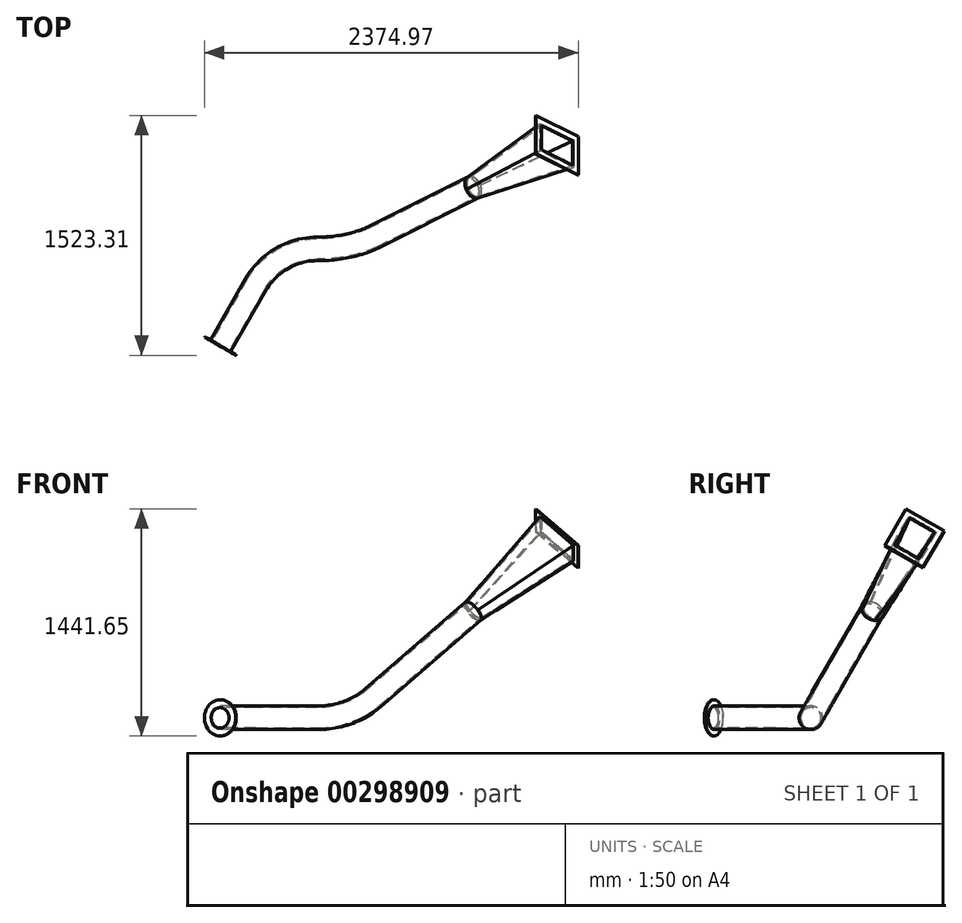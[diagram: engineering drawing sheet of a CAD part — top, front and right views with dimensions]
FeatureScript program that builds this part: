
annotation { "Feature Type Name" : "Feature", "Feature Type Description" : "" }
export const myFeature = defineFeature(function(context is Context, id is Id, definition is map)
    precondition{}
    {
        {
            var Q0;
            Q0=qCreatedBy(makeId("Right.planeOp"),FACE);
            var sketch = newSketch(context, id + "F0", { "sketchPlane" : qUnion([Q0])});
            skLineSegment(sketch, "E0", {"start": v(0, 0) * mm, "end": v(-42.12, 24.32) * mm});
            skSolve(sketch);
        }
        {
            var Q0;
            Q0=sQuery(id+"F0.wireOp",VERTEX,"E0.start");
            var Q1;
            Q1=sQuery(id+"F0.wireOp",EDGE,"E0");
            cPlane(context, id + "F1", {"entities" : qUnion([Q0, Q1]), "cplaneType" : CPlaneType.LINE_POINT, "offset" : 25 * mm, "width" : 150 * mm, "height" : 150 * mm});
        }
        {
            var Q0;
            Q0=qCreatedBy(makeId("Top.planeOp"),FACE);
            var sketch = newSketch(context, id + "F2", { "sketchPlane" : qUnion([Q0])});
            skArc(sketch, "E1", {"start": v(0, 0) * mm, "mid": v(-225, -60.29) * mm, "end": v(-389.71, -225) * mm});
            skLineSegment(sketch, "E2", {"start": v(0, 0) * mm, "end": v(0, -450) * mm, "construction": true});
            skLineSegment(sketch, "E3", {"start": v(-389.71, -225) * mm, "end": v(0, -450) * mm, "construction": true});
            skLineSegment(sketch, "E4", {"start": v(-389.71, -225) * mm, "end": v(-614.71, -614.71) * mm});
            skSolve(sketch);
        }
        {
            var Q0;
            Q0=qCreatedBy(id+"F1.planeOp",FACE);
            var sketch = newSketch(context, id + "F3", { "sketchPlane" : qUnion([Q0])});
            skArc(sketch, "E5", {"start": v(0, 0) * mm, "mid": v(191.34, 38.06) * mm, "end": v(353.55, 146.45) * mm});
            skLineSegment(sketch, "E6", {"start": v(0, 0) * mm, "end": v(0, 500) * mm, "construction": true});
            skLineSegment(sketch, "E7", {"start": v(0, 500) * mm, "end": v(353.55, 146.45) * mm, "construction": true});
            skLineSegment(sketch, "E8", {"start": v(353.55, 146.45) * mm, "end": v(989.95, 782.84) * mm});
            skSolve(sketch);
        }
        {
            var Q0;
            Q0=qCreatedBy(makeId("Right.planeOp"),FACE);
            var sketch = newSketch(context, id + "F4", { "sketchPlane" : qUnion([Q0])});
            skCircle(sketch, "E9", {"center": v(0, 0) * mm, "radius": 75 * mm});
            skSolve(sketch);
        }
        {
            var Q0;
            Q0=makeQuery(id+"F4.imprint","IMPRINT",FACE,{"disambiguationData":[TD([[makeQuery(id+"F4.imprint","IMPRINT",EDGE,{"derivedFrom":sQuery(id+"F4.wireOp",EDGE,"E9")}),1.0]])]});
            var Q1;
            Q1=sQuery(id+"F2.wireOp",EDGE,"E1");
            var Q2;
            Q2=sQuery(id+"F2.wireOp",EDGE,"E4");
            sweep(context, id + "F5", {"profiles" : qUnion([Q0]), "path" : qUnion([Q1, Q2])});
        }
        {
            var Q0;
            Q0=makeQuery(id+"F5.opSweep","CAP_FACE",FACE,{"disambiguationData":[OSD([sQuery(id+"F2.wireOp",VERTEX,"E1.start"),sQuery(id+"F4.wireOp",EDGE,"E9")])],"isStart":true});
            var Q1;
            Q1=sQuery(id+"F3.wireOp",EDGE,"E5");
            var Q2;
            Q2=sQuery(id+"F3.wireOp",EDGE,"E8");
            sweep(context, id + "F6", {"operationType" : NewBodyOperationType.ADD, "profiles" : qUnion([Q0]), "path" : qUnion([Q1, Q2])});
        }
        {
            var Q0;
            Q0=makeQuery(id+"F6.opSweep","CAP_FACE",FACE,{"disambiguationData":[OSD([sQuery(id+"F2.wireOp",VERTEX,"E1.start"),sQuery(id+"F3.wireOp",VERTEX,"E8.end"),sQuery(id+"F4.wireOp",EDGE,"E9")])],"isStart":false});
            cPlane(context, id + "F7", {"entities" : qUnion([Q0]), "cplaneType" : CPlaneType.OFFSET, "offset" : 750 * mm, "width" : 150 * mm, "height" : 150 * mm});
        }
        {
            var Q0;
            Q0=qCreatedBy(id+"F7.planeOp",FACE);
            var sketch = newSketch(context, id + "F8", { "sketchPlane" : qUnion([Q0])});
            skLineSegment(sketch, "E10", {"start": v(-91.24, 41.09) * mm, "end": v(93.93, -34.5) * mm});
            skLineSegment(sketch, "E11", {"start": v(93.93, -34.5) * mm, "end": v(-19.46, -312.25) * mm});
            skLineSegment(sketch, "E12", {"start": v(-19.46, -312.25) * mm, "end": v(-204.63, -236.66) * mm});
            skLineSegment(sketch, "E13", {"start": v(-204.63, -236.66) * mm, "end": v(-91.24, 41.09) * mm});
            skLineSegment(sketch, "E14", {"start": v(1.34, 3.29) * mm, "end": v(-55.35, -135.58) * mm, "construction": true});
            skLineSegment(sketch, "E15", {"start": v(-55.35, -135.58) * mm, "end": v(-147.93, -97.79) * mm, "construction": true});
            skSolve(sketch);
        }
        {
            var Q0;
            Q0=makeQuery(id+"F6.opSweep","CAP_FACE",FACE,{"disambiguationData":[OSD([sQuery(id+"F2.wireOp",VERTEX,"E1.start"),sQuery(id+"F3.wireOp",VERTEX,"E8.end"),sQuery(id+"F4.wireOp",EDGE,"E9")])],"isStart":false});
            var Q1;
            Q1=makeQuery(id+"F8.imprint","IMPRINT",FACE,{"disambiguationData":[TD([[makeQuery(id+"F8.imprint","IMPRINT",EDGE,{"derivedFrom":sQuery(id+"F8.wireOp",EDGE,"E10")}),-1.0]])]});
            loft(context, id + "F9", {"sheetProfilesArray" : [{ "sheetProfileEntities" : qUnion([Q0]) }, { "sheetProfileEntities" : qUnion([Q1]) }]});
        }
        {
            var Q0;
            Q0=makeQuery(id+"F9.opLoft","CAP_FACE",FACE,{"disambiguationData":[OSD([makeQuery(id+"F8.imprint","IMPRINT",FACE,{"disambiguationData":[TD([[makeQuery(id+"F8.imprint","IMPRINT",EDGE,{"derivedFrom":sQuery(id+"F8.wireOp",EDGE,"E10")}),-1.0]])]})])],"isStart":true});
            var Q1;
            Q1=makeQuery(id+"F5.opSweep","CAP_FACE",FACE,{"disambiguationData":[OSD([sQuery(id+"F2.wireOp",VERTEX,"E4.end"),sQuery(id+"F4.wireOp",EDGE,"E9")])],"isStart":false});
            shell(context, id + "F10", {"entities" : qUnion([Q0, Q1]), "thickness" : 10 * mm});
        }
        {
            var Q0;
            Q0=makeQuery(id+"F9.opLoft","CAP_FACE",FACE,{"disambiguationData":[OSD([makeQuery(id+"F8.imprint","IMPRINT",FACE,{"disambiguationData":[TD([[makeQuery(id+"F8.imprint","IMPRINT",EDGE,{"derivedFrom":sQuery(id+"F8.wireOp",EDGE,"E10")}),-1.0]])]})])],"isStart":true});
            var sketch = newSketch(context, id + "F11", { "sketchPlane" : qUnion([Q0])});
            skLineSegment(sketch, "E16", {"start": v(-113.15, 93.24) * mm, "end": v(146.08, -12.6) * mm});
            skLineSegment(sketch, "E17", {"start": v(146.08, -12.6) * mm, "end": v(2.45, -364.4) * mm});
            skLineSegment(sketch, "E18", {"start": v(2.45, -364.4) * mm, "end": v(-256.78, -258.57) * mm});
            skLineSegment(sketch, "E19", {"start": v(-256.78, -258.57) * mm, "end": v(-113.15, 93.24) * mm});
            skLineSegment(sketch, "E20", {"start": v(16.46, 40.32) * mm, "end": v(-55.35, -135.58) * mm, "construction": true});
            skLineSegment(sketch, "E21", {"start": v(-55.35, -135.58) * mm, "end": v(74.26, -188.5) * mm, "construction": true});
            skSolve(sketch);
        }
        {
            var Q0;
            Q0=makeQuery(id+"F11.imprint","IMPRINT",FACE,{"disambiguationData":[TD([[makeQuery(id+"F11.imprint","IMPRINT",EDGE,{"derivedFrom":sQuery(id+"F11.wireOp",EDGE,"E16")}),-1.0]])]});
            var Q1;
            {var subQ0=sQuery(id+"F8.wireOp",EDGE,"E13");var subQ2=sQuery(id+"F8.wireOp",EDGE,"E11");var subQ3=sQuery(id+"F8.wireOp",EDGE,"E10");Q1=makeQuery(id+"F11.imprint","IMPRINT",FACE,{"disambiguationData":[TD([[makeQuery(id+"F11.imprint","IMPRINT",EDGE,{"derivedFrom":makeQuery(id+"F9.opLoft","MID_CAP_EDGE",EDGE,{"disambiguationData":[OSD([subQ3,subQ2,subQ0])],"capPos":1.0})}),1.0]])]});}
            extrude(context, id + "F12", {"entities" : qUnion([Q0, Q1]), "depth" : 5 * mm});
        }
        {
            var Q0;
            Q0=makeQuery(id+"F5.opSweep","CAP_FACE",FACE,{"disambiguationData":[OSD([sQuery(id+"F2.wireOp",VERTEX,"E4.end"),sQuery(id+"F4.wireOp",EDGE,"E9")])],"isStart":false});
            var sketch = newSketch(context, id + "F13", { "sketchPlane" : qUnion([Q0])});
            skCircle(sketch, "E22", {"center": v(-225, 0) * mm, "radius": 115 * mm});
            skSolve(sketch);
        }
        {
            var Q0;
            Q0=makeQuery(id+"F13.imprint","IMPRINT",FACE,{"disambiguationData":[TD([[makeQuery(id+"F13.imprint","IMPRINT",EDGE,{"derivedFrom":sQuery(id+"F13.wireOp",EDGE,"E22")}),1.0]])]});
            var Q1;
            {var subQ0=sQuery(id+"F4.wireOp",EDGE,"E9");var subQ1=sQuery(id+"F2.wireOp",VERTEX,"E4.end");Q1=makeQuery(id+"F13.imprint","IMPRINT",FACE,{"disambiguationData":[TD([[makeQuery(id+"F13.imprint","IMPRINT",EDGE,{"derivedFrom":makeQuery(id+"F5.opSweep","CAP_EDGE",EDGE,{"disambiguationData":[OSD([subQ1,subQ0])],"isStart":false})}),1.0]])]});}
            extrude(context, id + "F14", {"entities" : qUnion([Q0, Q1]), "operationType" : NewBodyOperationType.ADD, "depth" : 5 * mm});
        }
    });
